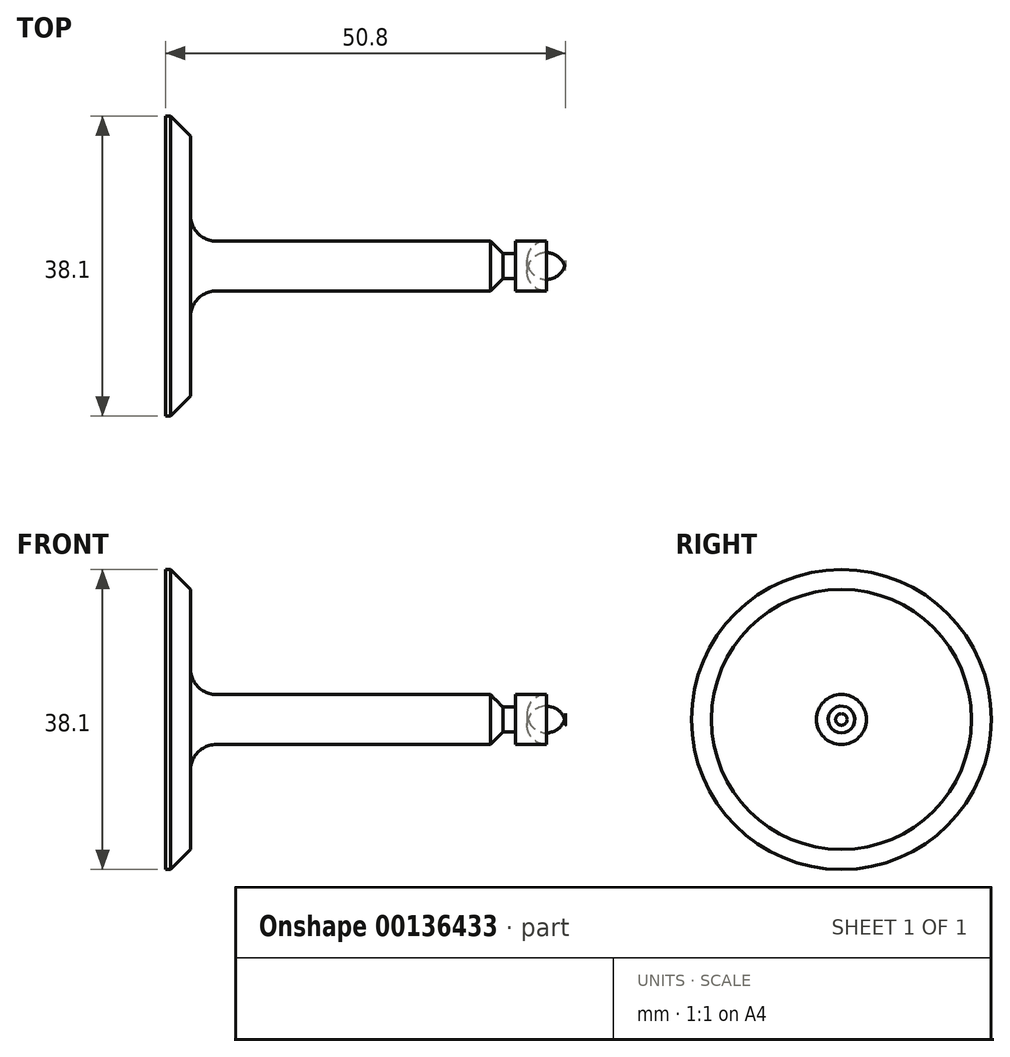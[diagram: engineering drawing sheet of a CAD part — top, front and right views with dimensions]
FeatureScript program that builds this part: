
annotation { "Feature Type Name" : "Feature", "Feature Type Description" : "" }
export const myFeature = defineFeature(function(context is Context, id is Id, definition is map)
    precondition{}
    {
        {
            var Q0;
            Q0=qCreatedBy(makeId("Front.planeOp"),FACE);
            var sketch = newSketch(context, id + "F0", { "sketchPlane" : qUnion([Q0])});
            skLineSegment(sketch, "E0", {"start": v(0, 0) * mm, "end": v(0, 3.17) * mm});
            skLineSegment(sketch, "E1", {"start": v(0, 3.17) * mm, "end": v(-6.35, 3.17) * mm});
            skLineSegment(sketch, "E2", {"start": v(-6.35, 3.17) * mm, "end": v(-6.35, 1.59) * mm});
            skLineSegment(sketch, "E3", {"start": v(-6.35, 1.59) * mm, "end": v(-7.95, 1.59) * mm});
            skLineSegment(sketch, "E4", {"start": v(-7.95, 1.59) * mm, "end": v(-7.95, 3.17) * mm});
            skLineSegment(sketch, "E5", {"start": v(-7.95, 3.17) * mm, "end": v(-47.62, 3.17) * mm});
            skLineSegment(sketch, "E6", {"start": v(-47.62, 3.17) * mm, "end": v(-47.62, 19.05) * mm});
            skLineSegment(sketch, "E7", {"start": v(-47.62, 19.05) * mm, "end": v(-50.8, 19.05) * mm});
            skLineSegment(sketch, "E8", {"start": v(-50.8, 19.05) * mm, "end": v(-50.8, 0) * mm});
            skLineSegment(sketch, "E9", {"start": v(-50.8, 0) * mm, "end": v(0, 0) * mm});
            skSolve(sketch);
        }
        {
            var Q0;
            Q0=makeQuery(id+"F0.imprint","IMPRINT",FACE,{"disambiguationData":[TD([[makeQuery(id+"F0.imprint","IMPRINT",EDGE,{"derivedFrom":sQuery(id+"F0.wireOp",EDGE,"E0")}),1.0]])]});
            var Q1;
            Q1=sQuery(id+"F0.wireOp",EDGE,"E9");
            revolve(context, id + "F1", {"entities" : qUnion([Q0]), "axis" : qUnion([Q1]), "revolveType" : RevolveType.FULL});
        }
        {
            var Q0;
            Q0=makeQuery(id+"F1.opRevolve","SWEPT_EDGE",EDGE,{"disambiguationData":[OSD([sQuery(id+"F0.wireOp",EDGE,"E5"),sQuery(id+"F0.wireOp",EDGE,"E6")])]});
            fillet(context, id + "F2", {"entities" : qUnion([Q0]), "radius" : 3.25 * mm, "tangentPropagation" : true, "allowEdgeOverflow" : false});
        }
        {
            var Q0;
            Q0=makeQuery(id+"F1.opRevolve","SWEPT_FACE",FACE,{"disambiguationData":[OSD([sQuery(id+"F0.wireOp",EDGE,"E6")])]});
            chamfer(context, id + "F3", {"entities" : qUnion([Q0]), "chamferType" : ChamferType.OFFSET_ANGLE, "width" : 2.54 * mm, "oppositeDirection" : false, "angle" : 45 * degree, "tangentPropagation" : true});
        }
        {
            var Q0;
            Q0=makeQuery(id+"F1.opRevolve","SWEPT_EDGE",EDGE,{"disambiguationData":[OSD([sQuery(id+"F0.wireOp",EDGE,"E4"),sQuery(id+"F0.wireOp",EDGE,"E5")])]});
            chamfer(context, id + "F4", {"entities" : qUnion([Q0]), "width" : 1.6 * mm});
        }
        {
            var Q0;
            Q0=makeQuery(id+"F1.opRevolve","SWEPT_EDGE",EDGE,{"disambiguationData":[OSD([sQuery(id+"F0.wireOp",EDGE,"E0"),sQuery(id+"F0.wireOp",EDGE,"E1")])]});
            fillet(context, id + "F5", {"entities" : qUnion([Q0]), "radius" : 2.44 * mm, "tangentPropagation" : true, "allowEdgeOverflow" : false});
        }
    });
